# Revit family: 5.Трубчатый шумоглушитель для круглых каналов SGK
name_source: partatom
category: Оборудование
revit_build: Autodesk Revit 2016 (Build: 20151209_0715(x64)
units: mm (PartAtom-declared; Revit-internal decimal feet)

## family parameters
Всегда вертикально = Да
На основе рабочей плоскости = Нет
Общий = Нет
При загрузке вырезать с полостями = Нет
Размер круглого соединителя = Использовать диаметр
Тип детали = Нормальный
Точка расчета площади = Нет

## types (12) — shared parameters
Единица измерения = шт.
Завод изготовитель = KORF
Ключевая пометка = Вентиляция
Материал = Сталь серая
Наименование и тех.хар-ка = Трубчатый шумоглушитель для круглых каналов
Раздел = ОВ

## per-type parameters (varying)
| type | B | А | Б | Д | Д1 | Масса единицы | Тип, марка, обозначение | отступ |
| 100/6 | 730 мм | 615 мм | 200 мм | 100 мм | 98 мм | 4 кг | SGK 100/6 | 60 мм |
| 125/6 | 730 мм | 615 мм | 225 мм | 125 мм | 123 мм | 4.8 кг | SGK 125/6 | 60 мм |
| 160/6 | 730 мм | 615 мм | 260 мм | 160 мм | 157 мм | 5,8 кг | SGK 160/6 | 60 мм |
| 200/6 | 730 мм | 615 мм | 300 мм | 200 мм | 196 мм | 6,4 кг | SGK 200/6 | 60 мм |
| 250/6 | 730 мм | 615 мм | 350 мм | 250 мм | 245 мм | 7,8 кг | SGK 250/6 | 60 мм |
| 315/6 | 730 мм | 615 мм | 455 мм | 315 мм | 309 мм | 10,4 кг | SGK 315/6 | 60 мм |
| 100/9 | 1030 мм | 915 мм | 200 мм | 100 мм | 98 мм | 5,4 кг | SGK 100/9 | 60 мм |
| 160/9 | 1030 мм | 915 мм | 260 мм | 160 мм | 157 мм | 7,4 кг | SGK 160/9 | 60 мм |
| 200/9 | 1030 мм | 915 мм | 300 мм | 200 мм | 196 мм | 9,2 кг | SGK 200/9 | 60 мм |
| 250/9 | 1030 мм | 915 мм | 350 мм | 250 мм | 245 мм | 10,6 кг | SGK 250/9 | 60 мм |
| 315/9 | 1030 мм | 915 мм | 455 мм | 315 мм | 309 мм | 14 кг | SGK 315/9 | 30 мм |
| 125/9 | 1030 мм | 915 мм | 225 мм | 125 мм | 123 мм | 6,6 кг | SGK 125/9 | 60 мм |
